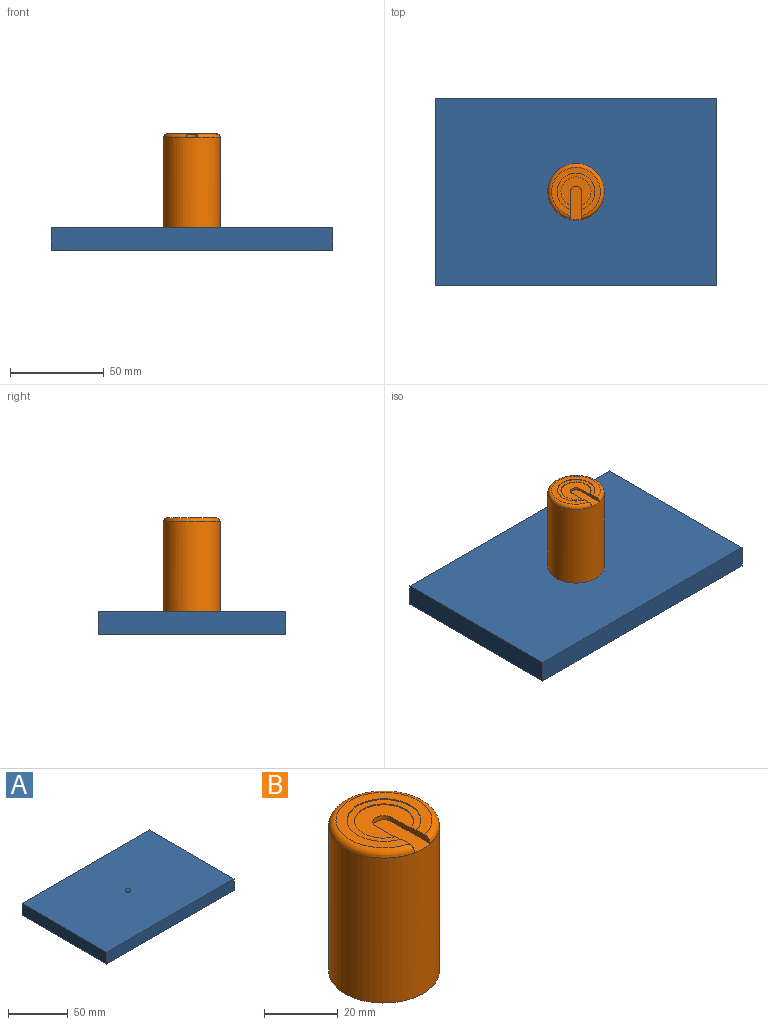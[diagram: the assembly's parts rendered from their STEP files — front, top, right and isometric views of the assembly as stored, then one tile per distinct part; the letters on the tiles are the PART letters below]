
ASSEMBLY  parts=2 mates=1
PART A: 8 faces, bbox 150x100x13 mm
  f0: plane 100x12mm, normal (-1,0,0), area 1200mm2, adj f1,f3,f4,f5
  f1: plane 150x12mm, normal (0,-1,0), area 1800mm2, adj f0,f2,f4,f5
  f2: plane 100x12mm, normal (1,0,0), area 1200mm2, adj f1,f3,f4,f5
  f3: plane 150x12mm, normal (0,1,0), area 1800mm2, adj f0,f2,f4,f5
  f4: plane 150x100mm, normal (0,0,1), area 14986.1mm2, adj f0,f1,f2,f3,f6
  f5: plane 150x100mm, normal (0,0,-1), area 15000mm2, adj f0,f1,f2,f3
  f6: cylinder r=2.1mm len=4.2mm, axis (0,0,-1), area 13.2mm2, adj f4,f7
  f7: plane 4.2x4.2mm, normal (0,0,1), area 13.9mm2, adj f6
PART B: 14 faces, bbox 32.5x32.1x50 mm
  f0: cylinder r=3mm len=6mm, axis (0,0,1), area 13.2mm2, adj f7,f8,f9,f13
  f1: plane 26x25.65mm, normal (0,0,1), area 198.6mm2, adj f2,f6,f7,f8
  f2: cylinder r=10mm len=20mm, axis (0,0,1), area 17mm2, adj f1,f3,f7,f8
  f3: plane 20x19.54mm, normal (0,0,1), area 100.9mm2, adj f2,f7,f8,f12
  f4: cylinder r=15mm len=48mm, axis (0,0,-1), area 4523.9mm2, adj f5,f6,f9
  f5: plane 30x30mm, normal (0,0,-1), area 693mm2, adj f4,f11
  f6: torus R=13mm, axis (0,0,1), area 262.8mm2, adj f1,f4,f7,f8
  f7: plane 14.7x2mm, normal (-1,0,0), area 23.4mm2, adj f0,f1,f2,f3,f6,f9,f12,f13
  f8: plane 14.7x2mm, normal (1,0,0), area 23.4mm2, adj f0,f1,f2,f3,f6,f9,f12,f13
  f9: plane 18x6mm, normal (0,0,1), area 103.5mm2, adj f0,f4,f7,f8
  f10: cone r=0mm half-angle=59deg, axis (0,0,-1), area 16.2mm2, adj f11
  f11: cylinder r=2.1mm len=10.4mm, axis (0,0,-1), area 137.2mm2, adj f5,f10
  f12: cylinder r=8mm len=16mm, axis (0,0,1), area 13.2mm2, adj f3,f7,f8,f13
  f13: plane 16x15.42mm, normal (0,0,1), area 140.1mm2, adj f0,f7,f8,f12
PLACE A t=(-3.47,-1.31,-2.59)mm
PLACE B t=(71.53,48.69,9.41)mm
MATE fastened B.f4 <-> A.f6  axis (0,0,-1) through (71.53,48.69,9.41)mm
